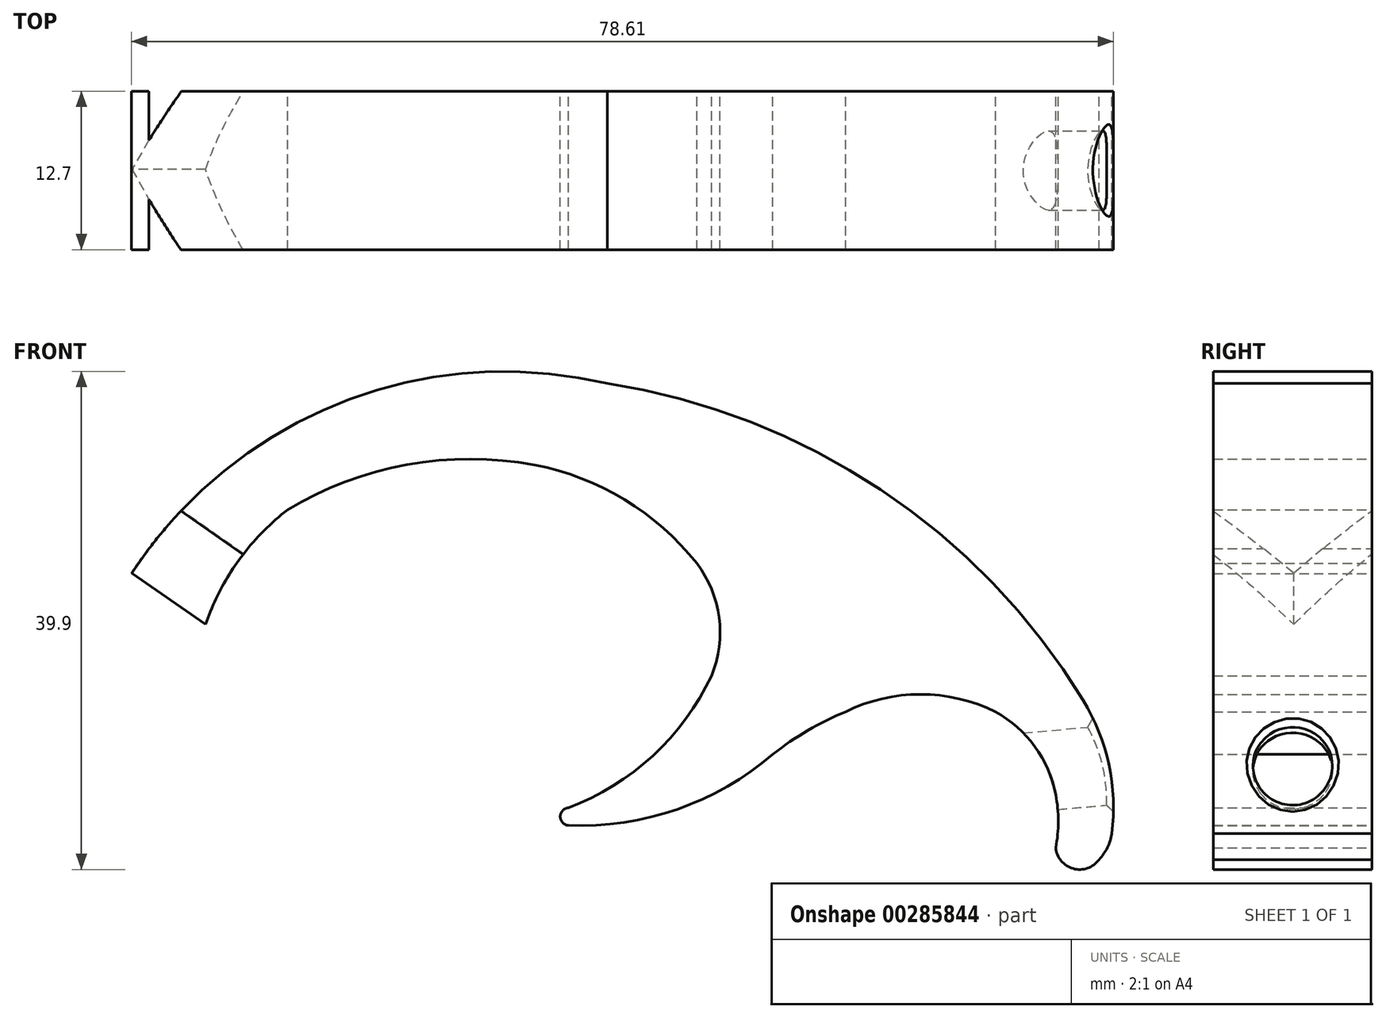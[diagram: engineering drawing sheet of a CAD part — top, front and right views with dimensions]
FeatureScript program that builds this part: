
annotation { "Feature Type Name" : "Feature", "Feature Type Description" : "" }
export const myFeature = defineFeature(function(context is Context, id is Id, definition is map)
    precondition{}
    {
        {
            var Q0;
            Q0=qCreatedBy(makeId("Front.planeOp"),FACE);
            var sketch = newSketch(context, id + "F0", { "sketchPlane" : qUnion([Q0])});
            skLineSegment(sketch, "E0", {"start": v(-79.66, 42.47) * mm, "end": v(-84.59, 51.35) * mm});
            skArc(sketch, "E1", {"start": v(-46.49, 66.6) * mm, "mid": v(-67.95, 65) * mm, "end": v(-84.59, 51.35) * mm});
            skArc(sketch, "E2", {"start": v(-8.39, 41.2) * mm, "mid": v(-24.63, 58.1) * mm, "end": v(-46.49, 66.6) * mm});
            skArc(sketch, "E3", {"start": v(-72.08, 56.48) * mm, "mid": v(-77.35, 50.27) * mm, "end": v(-79.66, 42.47) * mm});
            skArc(sketch, "E4", {"start": v(-52.32, 60.07) * mm, "mid": v(-62.53, 60.1) * mm, "end": v(-72.08, 56.48) * mm});
            skPoint(sketch, "E5.endSnap0", {"position": v(-24.63, 58.1) * mm});
            skArc(sketch, "E6", {"start": v(-10.6, 33.63) * mm, "mid": v(-12.26, 37.5) * mm, "end": v(-15.42, 40.3) * mm});
            skArc(sketch, "E7", {"start": v(-6.1, 30.53) * mm, "mid": v(-6.34, 36.05) * mm, "end": v(-8.39, 41.2) * mm});
            skArc(sketch, "E8", {"start": v(-7.14, 28.45) * mm, "mid": v(-6.46, 29.4) * mm, "end": v(-6.1, 30.53) * mm});
            skArc(sketch, "E9", {"start": v(-10.6, 29.4) * mm, "mid": v(-10.39, 31.52) * mm, "end": v(-10.6, 33.63) * mm});
            skPoint(sketch, "E9.startSnap0", {"position": v(-6.46, 29.4) * mm});
            skArc(sketch, "E10", {"start": v(-10.6, 29.4) * mm, "mid": v(-9.2, 27.73) * mm, "end": v(-7.14, 28.45) * mm});
            skArc(sketch, "E11", {"start": v(-39.33, 52.18) * mm, "mid": v(-45.12, 57.3) * mm, "end": v(-52.32, 60.07) * mm});
            skArc(sketch, "E12", {"start": v(-15.42, 40.3) * mm, "mid": v(-21.42, 41.7) * mm, "end": v(-27.42, 40.3) * mm});
            skArc(sketch, "E13", {"start": v(-27.42, 40.3) * mm, "mid": v(-30.45, 38.8) * mm, "end": v(-33.24, 36.89) * mm});
            skArc(sketch, "E14", {"start": v(-49.61, 31.2) * mm, "mid": v(-40.89, 32.48) * mm, "end": v(-33.24, 36.89) * mm});
            skArc(sketch, "E15", {"start": v(-49.61, 32.6) * mm, "mid": v(-50.27, 31.9) * mm, "end": v(-49.61, 31.2) * mm});
            skArc(sketch, "E16", {"start": v(-49.61, 32.6) * mm, "mid": v(-42.85, 36.77) * mm, "end": v(-38.15, 43.19) * mm});
            skArc(sketch, "E17", {"start": v(-38.15, 43.19) * mm, "mid": v(-37.55, 47.84) * mm, "end": v(-39.33, 52.18) * mm});
            skSolve(sketch);
        }
        {
            var Q0;
            Q0 = qSketchRegion(id + "F0", true);
            extrude(context, id + "F1", {"entities" : qUnion([Q0]), "depth" : 12.7 * mm});
        }
        {
            var Q0;
            Q0=makeQuery(id+"F1.opExtrude","SWEPT_EDGE",EDGE,{"disambiguationData":[OSD([sQuery(id+"F0.wireOp",EDGE,"E0"),sQuery(id+"F0.wireOp",EDGE,"E1")])]});
            cPlane(context, id + "F2", {"entities" : qUnion([Q0]), "cplaneType" : CPlaneType.LINE_ANGLE, "offset" : 25.4 * mm, "angle" : 125 * degree, "width" : 152.4 * mm, "height" : 152.4 * mm});
        }
        {
            var Q0;
            Q0=qCreatedBy(id+"F2.planeOp",FACE);
            var sketch = newSketch(context, id + "F3", { "sketchPlane" : qUnion([Q0])});
            skLineSegment(sketch, "E18", {"start": v(0, 0) * mm, "end": v(-6.26, -6.38) * mm});
            skLineSegment(sketch, "E19", {"start": v(-6.26, -6.38) * mm, "end": v(-12.76, 0) * mm});
            skLineSegment(sketch, "E20", {"start": v(-12.76, 0) * mm, "end": v(-18.1, -16.76) * mm});
            skLineSegment(sketch, "E21", {"start": v(-18.1, -16.76) * mm, "end": v(3.4, -16.76) * mm});
            skLineSegment(sketch, "E22", {"start": v(3.4, -16.76) * mm, "end": v(0, 0) * mm});
            skSolve(sketch);
        }
        {
            var Q0;
            Q0=makeQuery(id+"F3.imprint","IMPRINT",FACE,{"disambiguationData":[TD([[makeQuery(id+"F3.imprint","IMPRINT",EDGE,{"derivedFrom":sQuery(id+"F3.wireOp",EDGE,"E18")}),1.0]])]});
            extrude(context, id + "F4", {"entities" : qUnion([Q0]), "operationType" : NewBodyOperationType.REMOVE, "depth" : 24.13 * mm});
        }
        {
            var Q0;
            Q0=makeQuery(id+"F1.opExtrude","SWEPT_EDGE",EDGE,{"disambiguationData":[OSD([sQuery(id+"F0.wireOp",EDGE,"E7"),sQuery(id+"F0.wireOp",EDGE,"E8")])]});
            cPlane(context, id + "F5", {"entities" : qUnion([Q0]), "cplaneType" : CPlaneType.LINE_ANGLE, "offset" : 25.4 * mm, "angle" : 85 * degree, "width" : 152.4 * mm, "height" : 152.4 * mm});
        }
        {
            var Q0;
            Q0=qCreatedBy(id+"F5.planeOp",FACE);
            var sketch = newSketch(context, id + "F6", { "sketchPlane" : qUnion([Q0])});
            skCircle(sketch, "E23", {"center": v(-6.35, 36.43) * mm, "radius": 3.18 * mm});
            skSolve(sketch);
        }
        {
            var Q0;
            Q0=makeQuery(id+"F6.imprint","IMPRINT",FACE,{"disambiguationData":[TD([[makeQuery(id+"F6.imprint","IMPRINT",EDGE,{"derivedFrom":sQuery(id+"F6.wireOp",EDGE,"E23")}),1.0]])]});
            extrude(context, id + "F7", {"entities" : qUnion([Q0]), "operationType" : NewBodyOperationType.REMOVE, "endBound" : BoundingType.SYMMETRIC, "oppositeDirection" : true, "depth" : 17.27 * mm});
        }
        {
            var Q0;
            Q0=makeQuery(id+"F7.boolean.opBoolean","INTERSECT",EDGE,{"derivedFrom":[makeQuery(id+"F1.opExtrude","SWEPT_FACE",FACE,{"disambiguationData":[OSD([sQuery(id+"F0.wireOp",EDGE,"E7")])]}),makeQuery(id+"F7.opExtrude","SWEPT_FACE",FACE,{"disambiguationData":[OSD([sQuery(id+"F6.wireOp",EDGE,"E23")])]})]});
            chamfer(context, id + "F8", {"entities" : qUnion([Q0]), "width" : 0.5 * mm, "tangentPropagation" : true});
        }
    });
